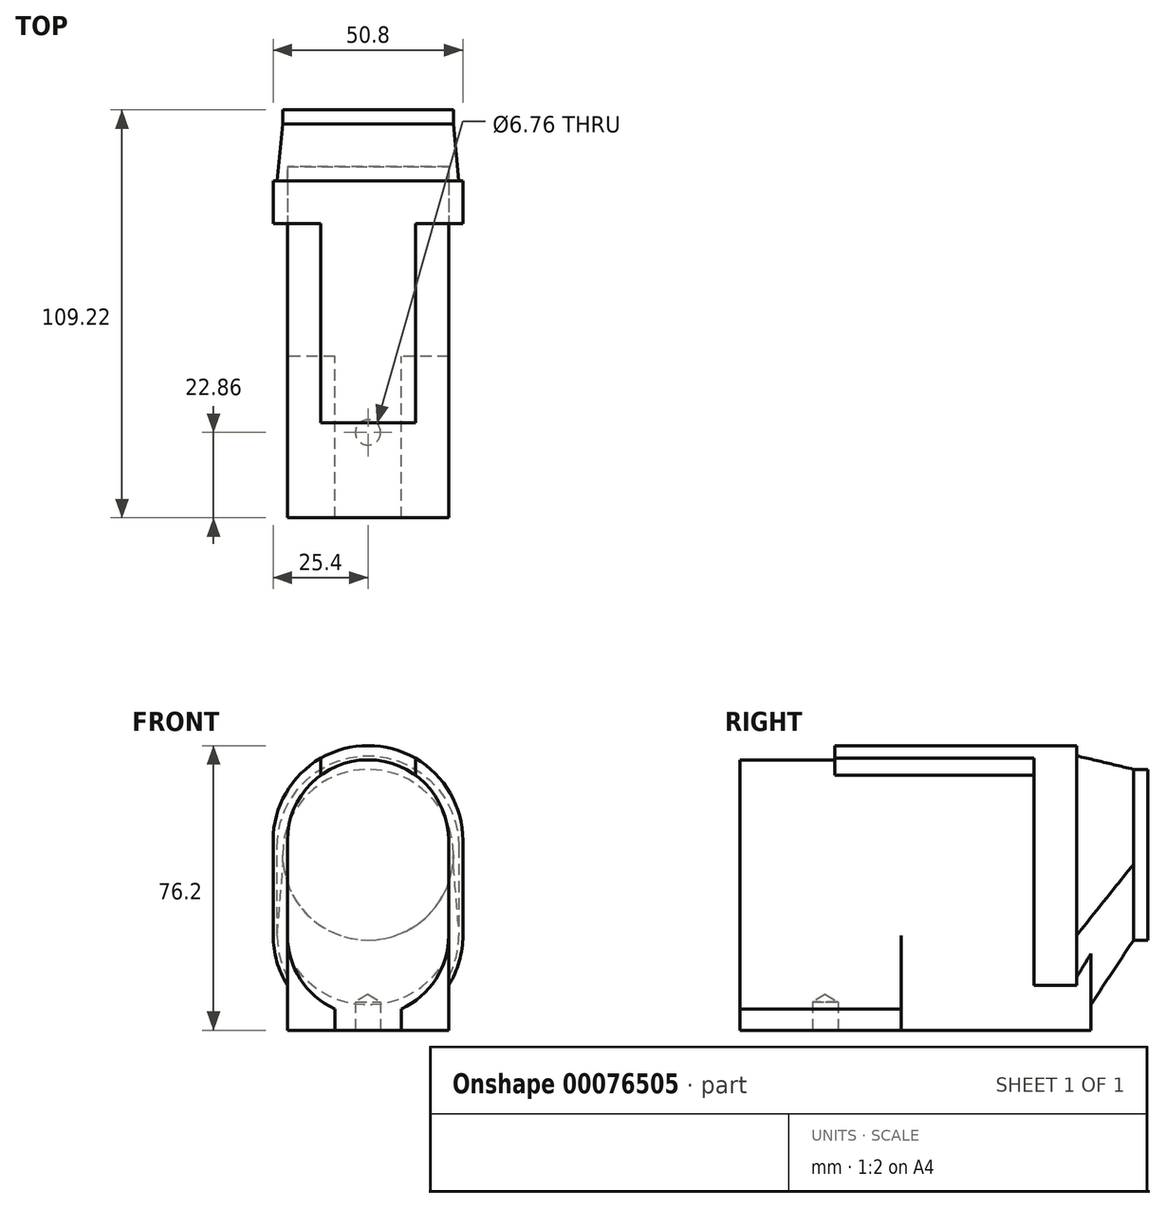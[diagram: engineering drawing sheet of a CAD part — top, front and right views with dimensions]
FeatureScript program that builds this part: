
annotation { "Feature Type Name" : "Feature", "Feature Type Description" : "" }
export const myFeature = defineFeature(function(context is Context, id is Id, definition is map)
    precondition{}
    {
        {
            var Q0;
            Q0=qCreatedBy(makeId("Front.planeOp"),FACE);
            var sketch = newSketch(context, id + "F0", { "sketchPlane" : qUnion([Q0])});
            skArc(sketch, "E0", {"start": v(-21.6, -12.7) * mm, "mid": v(0, -34.3) * mm, "end": v(21.6, -12.7) * mm});
            skArc(sketch, "E1", {"start": v(21.6, 12.7) * mm, "mid": v(0, 34.3) * mm, "end": v(-21.59, 12.7) * mm});
            skLineSegment(sketch, "E2", {"start": v(21.59, 12.7) * mm, "end": v(21.59, 0) * mm});
            skLineSegment(sketch, "E3", {"start": v(-21.59, -12.7) * mm, "end": v(-21.59, 12.7) * mm});
            skLineSegment(sketch, "E4", {"start": v(21.59, 0) * mm, "end": v(21.6, -12.7) * mm});
            skSolve(sketch);
        }
        {
            var Q0;
            Q0 = qSketchRegion(id + "F0", true);
            extrude(context, id + "F1", {"entities" : qUnion([Q0]), "depth" : 78.74 * mm});
        }
        {
            var Q0;
            Q0=qCreatedBy(makeId("Front.planeOp"),FACE);
            cPlane(context, id + "F2", {"entities" : qUnion([Q0]), "cplaneType" : CPlaneType.OFFSET, "offset" : 26.67 * mm, "oppositeDirection" : true, "width" : 152.4 * mm, "height" : 152.4 * mm});
        }
        {
            var Q0;
            Q0=qCreatedBy(id+"F2.planeOp",FACE);
            var sketch = newSketch(context, id + "F3", { "sketchPlane" : qUnion([Q0])});
            skArc(sketch, "E5", {"start": v(22.86, 8.89) * mm, "mid": v(0, 31.75) * mm, "end": v(-22.86, 8.89) * mm});
            skArc(sketch, "E6", {"start": v(22.72, 6.35) * mm, "mid": v(22.82, 7.62) * mm, "end": v(22.86, 8.89) * mm});
            skArc(sketch, "E7", {"start": v(-22.86, 8.89) * mm, "mid": v(-22.82, 7.62) * mm, "end": v(-22.72, 6.35) * mm});
            skArc(sketch, "E8", {"start": v(-22.72, 6.35) * mm, "mid": v(0, -13.97) * mm, "end": v(22.72, 6.35) * mm});
            skLineSegment(sketch, "E9", {"start": v(22.86, 8.89) * mm, "end": v(-22.86, 8.89) * mm});
            skLineSegment(sketch, "E10", {"start": v(22.72, 6.35) * mm, "end": v(-22.72, 6.35) * mm});
            skSolve(sketch);
        }
        {
            var Q0;
            Q0=qCreatedBy(makeId("Front.planeOp"),FACE);
            var sketch = newSketch(context, id + "F4", { "sketchPlane" : qUnion([Q0])});
            skArc(sketch, "E11", {"start": v(25.4, 12.7) * mm, "mid": v(0, 38.1) * mm, "end": v(-25.4, 12.7) * mm});
            skArc(sketch, "E12", {"start": v(-25.4, -12.7) * mm, "mid": v(0, -38.1) * mm, "end": v(25.4, -12.7) * mm});
            skLineSegment(sketch, "E13", {"start": v(25.4, 12.7) * mm, "end": v(25.4, -12.7) * mm});
            skLineSegment(sketch, "E14", {"start": v(-25.4, -12.7) * mm, "end": v(-25.4, 12.7) * mm});
            skLineSegment(sketch, "E15", {"start": v(25.4, 12.7) * mm, "end": v(-25.4, 12.7) * mm});
            skLineSegment(sketch, "E16", {"start": v(-25.4, -12.7) * mm, "end": v(25.4, -12.7) * mm});
            skSolve(sketch);
        }
        {
            var Q1;
            Q1=makeQuery(id+"F4.imprint","IMPRINT",FACE,{"disambiguationData":[TD([[makeQuery(id+"F4.imprint","IMPRINT",EDGE,{"derivedFrom":sQuery(id+"F4.wireOp",EDGE,"E11")}),1.0]])]});
            var Q2;
            Q2=makeQuery(id+"F3.imprint","IMPRINT",FACE,{"disambiguationData":[TD([[makeQuery(id+"F3.imprint","IMPRINT",EDGE,{"derivedFrom":sQuery(id+"F3.wireOp",EDGE,"E5")}),1.0]])]});
            var Q3;
            Q3=makeQuery(id+"F6.opExtrude","CAP_VERTEX",VERTEX,{"disambiguationData":[OSD([sQuery(id+"F4.wireOp",EDGE,"E11"),sQuery(id+"F4.wireOp",EDGE,"E13")])],"isStart":false});
            var Q4;
            Q4=sQuery(id+"F3.wireOp",VERTEX,"E5.start");
            loft(context, id + "F5", {"operationType" : NewBodyOperationType.ADD, "sheetProfilesArray" : [{ "sheetProfileEntities" : qUnion([Q1]) }, { "sheetProfileEntities" : qUnion([Q2]) }], "connections" : [{ "connectionEntities" : qUnion([Q3, Q4]), "connectionEdgeQueries" : qUnion([]), "connectionEdgeParameters" : [] }]});
        }
        {
            var Q0;
            Q0 = qSketchRegion(id + "F4", true);
            extrude(context, id + "F6", {"entities" : qUnion([Q0]), "operationType" : NewBodyOperationType.ADD, "oppositeDirection" : true, "depth" : 11.43 * mm});
        }
        {
            var Q0;
            Q0=makeQuery(id+"F6.opExtrude","CAP_FACE",FACE,{"disambiguationData":[OSD([sQuery(id+"F4.wireOp",EDGE,"E11"),sQuery(id+"F4.wireOp",EDGE,"E12"),sQuery(id+"F4.wireOp",EDGE,"E13"),sQuery(id+"F4.wireOp",EDGE,"E14")])],"isStart":false});
            var sketch = newSketch(context, id + "F7", { "sketchPlane" : qUnion([Q0])});
            skArc(sketch, "E17", {"start": v(-24.31, -12.7) * mm, "mid": v(0, -37.01) * mm, "end": v(24.31, -12.7) * mm});
            skLineSegment(sketch, "E18", {"start": v(-24.31, 11.07) * mm, "end": v(-24.31, -12.7) * mm});
            skLineSegment(sketch, "E19", {"start": v(-24.31, -12.7) * mm, "end": v(24.31, -12.7) * mm});
            skLineSegment(sketch, "E20", {"start": v(24.31, -12.7) * mm, "end": v(24.31, 11.07) * mm});
            skLineSegment(sketch, "E21", {"start": v(-24.31, 11.07) * mm, "end": v(24.31, 11.07) * mm});
            skSolve(sketch);
        }
        {
            var Q1;
            Q1=makeQuery(id+"F7.imprint","IMPRINT",FACE,{"disambiguationData":[TD([[makeQuery(id+"F7.imprint","IMPRINT",EDGE,{"derivedFrom":sQuery(id+"F7.wireOp",EDGE,"E18")}),1.0]])]});
            var Q2;
            Q2=makeQuery(id+"F3.imprint","IMPRINT",FACE,{"disambiguationData":[TD([[makeQuery(id+"F3.imprint","IMPRINT",EDGE,{"derivedFrom":sQuery(id+"F3.wireOp",EDGE,"E6")}),1.0]])]});
            loft(context, id + "F8", {"operationType" : NewBodyOperationType.ADD, "sheetProfilesArray" : [{ "sheetProfileEntities" : qUnion([Q1]) }, { "sheetProfileEntities" : qUnion([Q2]) }]});
        }
        {
            var Q1;
            Q1=makeQuery(id+"F3.imprint","IMPRINT",FACE,{"disambiguationData":[TD([[makeQuery(id+"F3.imprint","IMPRINT",EDGE,{"derivedFrom":sQuery(id+"F3.wireOp",EDGE,"E8")}),1.0]])]});
            var Q2;
            Q2=makeQuery(id+"F7.imprint","IMPRINT",FACE,{"disambiguationData":[TD([[makeQuery(id+"F7.imprint","IMPRINT",EDGE,{"derivedFrom":sQuery(id+"F7.wireOp",EDGE,"E17")}),1.0]])]});
            loft(context, id + "F9", {"operationType" : NewBodyOperationType.ADD, "sheetProfilesArray" : [{ "sheetProfileEntities" : qUnion([Q1]) }, { "sheetProfileEntities" : qUnion([Q2]) }]});
        }
        {
            var Q0;
            Q0 = qSketchRegion(id + "F3", true);
            extrude(context, id + "F10", {"entities" : qUnion([Q0]), "operationType" : NewBodyOperationType.ADD, "oppositeDirection" : true, "depth" : 3.8 * mm});
        }
        {
            var Q0;
            Q0=qCreatedBy(makeId("Front.planeOp"),FACE);
            var sketch = newSketch(context, id + "F11", { "sketchPlane" : qUnion([Q0])});
            skArc(sketch, "E22.0", {"start": v(12.7, 34.7) * mm, "mid": v(0, 38.1) * mm, "end": v(-12.7, 34.7) * mm});
            skLineSegment(sketch, "E23.top", {"start": v(-12.7, 12.7) * mm, "end": v(12.7, 12.7) * mm});
            skLineSegment(sketch, "E23.left", {"start": v(-12.7, 34.7) * mm, "end": v(-12.7, 12.7) * mm});
            skLineSegment(sketch, "E23.right", {"start": v(12.7, 34.7) * mm, "end": v(12.7, 12.7) * mm});
            skSolve(sketch);
        }
        {
            var Q0;
            Q0 = qSketchRegion(id + "F11", true);
            extrude(context, id + "F12", {"entities" : qUnion([Q0]), "operationType" : NewBodyOperationType.ADD, "depth" : 53.34 * mm});
        }
        {
            var Q0;
            Q0=qCreatedBy(makeId("Top.planeOp"),FACE);
            var sketch = newSketch(context, id + "F13", { "sketchPlane" : qUnion([Q0])});
            skLineSegment(sketch, "E24.bottom", {"start": v(21.6, 15.24) * mm, "end": v(-21.59, 15.24) * mm});
            skLineSegment(sketch, "E24.top", {"start": v(21.6, -35.56) * mm, "end": v(8.9, -35.56) * mm});
            skLineSegment(sketch, "E24.left", {"start": v(21.59, 15.24) * mm, "end": v(21.6, -35.56) * mm});
            skLineSegment(sketch, "E24.right", {"start": v(-21.6, 15.24) * mm, "end": v(-21.59, -35.56) * mm});
            skLineSegment(sketch, "E25.top", {"start": v(8.9, -78.74) * mm, "end": v(-8.89, -78.74) * mm});
            skLineSegment(sketch, "E25.left", {"start": v(8.9, -35.56) * mm, "end": v(8.9, -78.74) * mm});
            skLineSegment(sketch, "E25.right", {"start": v(-8.89, -35.56) * mm, "end": v(-8.89, -78.74) * mm});
            skLineSegment(sketch, "E26.trimOffspring", {"start": v(-8.89, -35.56) * mm, "end": v(-21.59, -35.56) * mm});
            skSolve(sketch);
        }
        {
            var Q0;
            Q0 = qSketchRegion(id + "F13", true);
            extrude(context, id + "F14", {"entities" : qUnion([Q0]), "operationType" : NewBodyOperationType.ADD, "oppositeDirection" : true, "depth" : 38.1 * mm});
        }
        {
            var Q0;
            Q0=makeQuery(id+"F14.opExtrude","CAP_FACE",FACE,{"disambiguationData":[OSD([sQuery(id+"F13.wireOp",EDGE,"E24.bottom"),sQuery(id+"F13.wireOp",EDGE,"E24.top"),sQuery(id+"F13.wireOp",EDGE,"E24.left"),sQuery(id+"F13.wireOp",EDGE,"E24.right"),sQuery(id+"F13.wireOp",EDGE,"E25.top"),sQuery(id+"F13.wireOp",EDGE,"E25.left"),sQuery(id+"F13.wireOp",EDGE,"E25.right"),sQuery(id+"F13.wireOp",EDGE,"E26.trimOffspring")])],"isStart":false});
            var sketch = newSketch(context, id + "F15", { "sketchPlane" : qUnion([Q0])});
            skCircle(sketch, "E27", {"center": v(0, 55.88) * mm, "radius": 3.04 * mm});
            skPoint(sketch, "E27.centerSnap0", {"position": v(0, 78.74) * mm});
            skSolve(sketch);
        }
        {
            var Q0;
            Q0=sQuery(id+"F15.wireOp",VERTEX,"E27.center");
            var Q1;
            Q1=makeQuery(id+"F1.opExtrude","SWEPT_BODY",BODY,{"disambiguationData":[OSD([sQuery(id+"F0.wireOp",EDGE,"E0"),sQuery(id+"F0.wireOp",EDGE,"E1"),sQuery(id+"F0.wireOp",EDGE,"E2"),sQuery(id+"F0.wireOp",EDGE,"E3"),sQuery(id+"F0.wireOp",EDGE,"E4")])]});
            hole(context, id + "F16", {"style" : HoleStyle.SIMPLE, "endStyle" : HoleEndStyle.BLIND, "standardTappedOrClearance" : lookupTablePath({ "standard" : "ANSI", "fit" : "Normal (ASME)", "size" : "1/4", "type" : "Clearance" }), "standardBlindInLast" : lookupTablePath({ "fit" : "Free", "standard" : "ANSI", "size" : "1/4", "type" : "Clearance" }), "holeDiameter" : 6.76 * mm, "holeDepth" : 7.62 * mm, "startFromSketch" : true, "locations" : qUnion([Q0]), "scope" : qUnion([Q1])});
        }
    });
